# Revit family: FU_Stool_Sandler_Ring 3-1
name_source: partatom
category: Furniture
units: mm (PartAtom-declared; Revit-internal decimal feet)

## family parameters
Always vertical = Yes
Cut with Voids When Loaded = No
OmniClass Number = 23.40.20.00
OmniClass Title = General Furniture and Specialties
Room Calculation Point = No
Shared = No
Work Plane-Based = No

## types (1)
- Ring 3.1
    Default Elevation = 0 mm  [stored 0 ft]
    Depth = 510 mm  [stored 1.67323 ft]
    Description = Upholstered bar stool on steel frame.
    Frame = Sandler - Frame - Polished Aluminium
    Height = 970 mm  [stored 3.18241 ft]
    Manufacturer = Sandler
    Model = Ring 3.1
    Seat = Fabric - Mainline Flax - Monument MLF09
    URL = https://www.sandlerseating.com
    Width = 520 mm  [stored 1.70604 ft]

note: [stored X ft] marks values corroborated as IEEE doubles in the binary element streams (Revit-internal decimal feet)

## geometry (parser evidence)
native form markers: Sweep x3
no freeform markers — native parametric forms only
